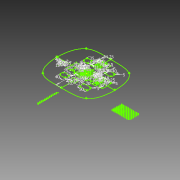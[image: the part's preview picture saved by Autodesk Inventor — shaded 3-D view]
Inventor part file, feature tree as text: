
AUTODESK INVENTOR PART (.ipt)
format: ipt  version: 2012 (Build 160160000, 160)  size: 232,448 bytes
history: native  units: mm
features: sketch x1
ambient origin geometry x8: Origin, YZ Plane, XZ Plane, XY Plane, X Axis, Y Axis, Z Axis, Center Point
feature tree (1):
  sketch  "Sketch1"  dims[d50=300.0mm d51=3.0mm d52=33.0mm d53=33.0mm d54=3.0mm d55=34.25mm d56=25.275mm d58=27.0mm d59=71.0mm d60=20.0mm d61=20.0mm d62=25.275mm d63=3.0mm d64=3.0mm d65=2.5mm d66=3.3mm d67=22.0mm d68=3.3mm d69=3.0mm d70=18.0mm d71=18.0mm d72=32.0mm d73=35.5mm d74=60.0mm d75=70.0mm d76=3.0mm d77=3.0mm d78=51.0mm d79=4.5mm d80=20.0mm d81=4.5mm d82=51.0mm d83=5.0mm d84=5.0mm d85=5.0mm d86=5.0mm d87=10.0mm d88=30.0mm d89=30.0mm d90=25.0mm d91=25.0mm d92=5.0mm d93=9.5mm d94=51.0mm d95=9.5mm d96=51.0mm d97=25.0mm d98=30.0mm d99=30.0mm d100=33.0mm d116=64.0mm d117=3.0mm d118=3.0mm d119=3.0mm d120=3.0mm d121=3.0mm d122=5.632993mm d125=4.7mm d126=5.0mm d128=10.0mm d129=5.0mm d130=10.0mm d131=5.0mm d132=66.0mm d134=3.0mm d135=3.0mm d137=3.0mm d138=5.682993mm d139=4.7mm d140=5.0mm d141=10.0mm d142=5.0mm d143=3.0mm d144=5.0mm d145=5.0mm d146=12.0mm d147=30.0mm d148=5.0mm d150=3.0mm d153=3.0mm d154=8.0mm d155=6.0mm d156=6.0mm d160=36.2mm d161=8.0mm d162=50.0mm d163=5.0mm d164=40.0mm d165=28.5mm d166=5.0mm d167=15.0mm d168=3.1mm d169=15.0mm d170=5.0mm d171=35.0mm d172=5.0mm d173=40.0mm d177=66.0mm d182=40.0mm d183=10.0mm]
